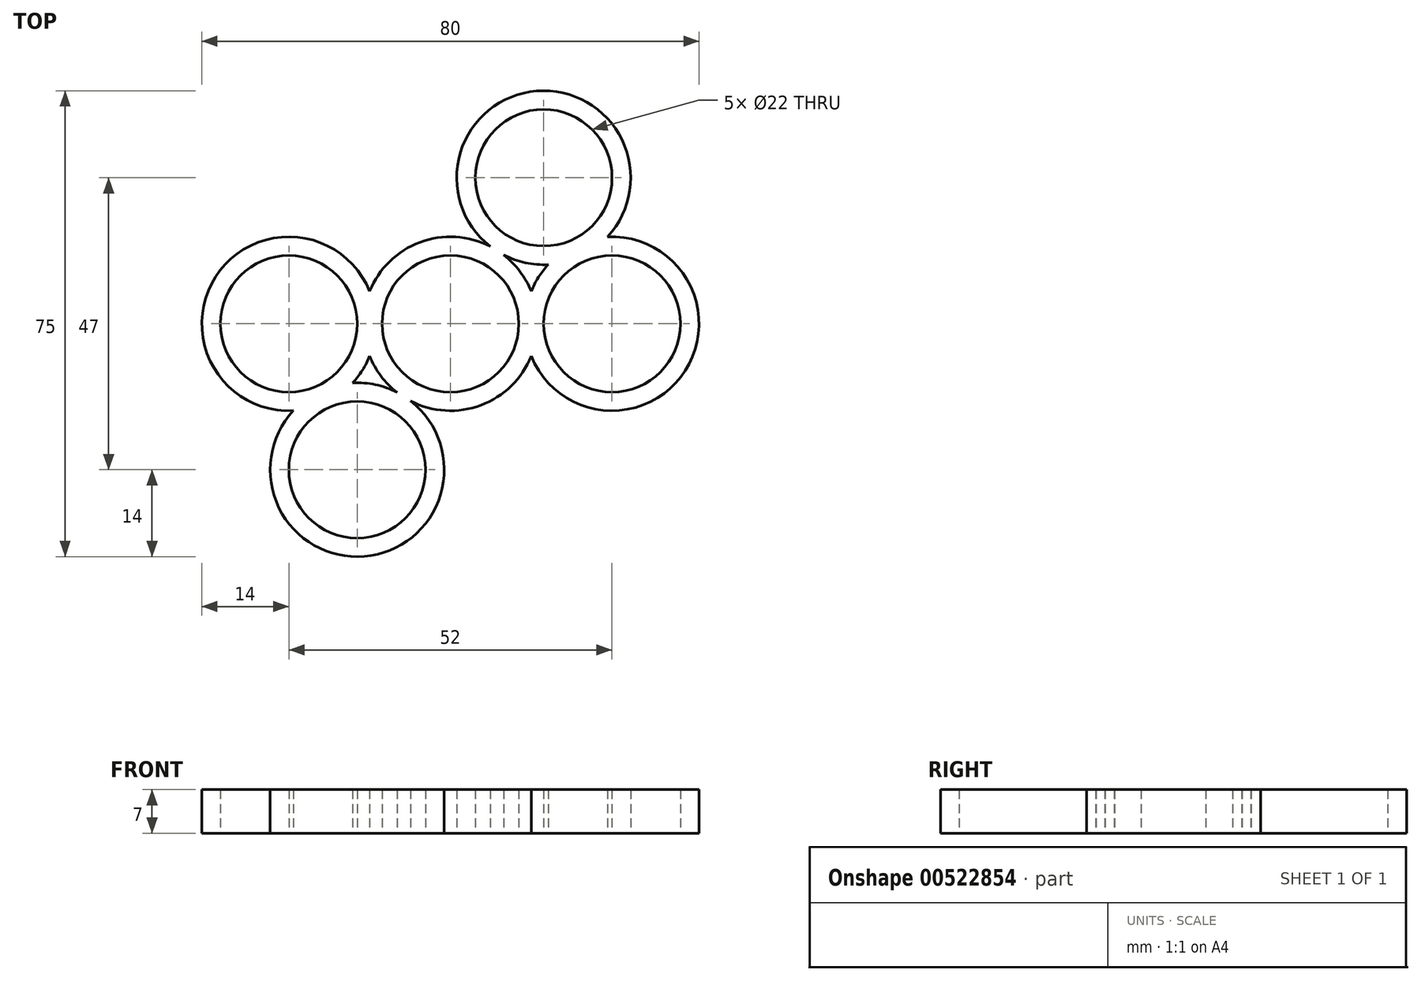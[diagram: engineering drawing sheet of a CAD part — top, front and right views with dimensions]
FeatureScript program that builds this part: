
annotation { "Feature Type Name" : "Feature", "Feature Type Description" : "" }
export const myFeature = defineFeature(function(context is Context, id is Id, definition is map)
    precondition{}
    {
        {
            var Q0;
            Q0=qCreatedBy(makeId("Top.planeOp"),FACE);
            var sketch = newSketch(context, id + "F0", { "sketchPlane" : qUnion([Q0])});
            skCircle(sketch, "E0", {"center": v(0, 0) * mm, "radius": 11 * mm});
            skCircle(sketch, "E1", {"center": v(26, 0) * mm, "radius": 11 * mm});
            skCircle(sketch, "E2", {"center": v(26, 0) * mm, "radius": 14 * mm});
            skCircle(sketch, "E3", {"center": v(0, 0) * mm, "radius": 14 * mm});
            skCircle(sketch, "E4", {"center": v(15, 23.5) * mm, "radius": 11 * mm});
            skCircle(sketch, "E5", {"center": v(15, 23.5) * mm, "radius": 14 * mm});
            skCircle(sketch, "E6", {"center": v(-26, 0) * mm, "radius": 11 * mm});
            skCircle(sketch, "E7", {"center": v(-26, 0) * mm, "radius": 14 * mm});
            skCircle(sketch, "E8", {"center": v(-15, -23.5) * mm, "radius": 11 * mm});
            skCircle(sketch, "E9", {"center": v(-15, -23.5) * mm, "radius": 14 * mm});
            skLineSegment(sketch, "E10", {"start": v(-1, -23.5) * mm, "end": v(-1, -13.96) * mm});
            skLineSegment(sketch, "E11", {"start": v(1, 23.5) * mm, "end": v(1, 13.96) * mm});
            skSolve(sketch);
        }
        {
            var Q0;
            Q0=makeQuery(id+"F0.imprint","IMPRINT",FACE,{"disambiguationData":[TD([[makeQuery(id+"F0.imprint","IMPRINT",EDGE,{"derivedFrom":sQuery(id+"F0.wireOp",EDGE,"E6")}),-1.0]])]});
            var Q1;
            Q1=makeQuery(id+"F0.imprint","IMPRINT",FACE,{"disambiguationData":[TD([[makeQuery(id+"F0.imprint","IMPRINT",EDGE,{"derivedFrom":sQuery(id+"F0.wireOp",EDGE,"E0")}),-1.0]])]});
            var Q2;
            {var subQ0=sQuery(id+"F0.wireOp",EDGE,"E7");var subQ1=sQuery(id+"F0.wireOp",EDGE,"E3");var subQ2=makeQuery(id+"F0.imprint","INTERSECT",VERTEX,{"disambiguationData":[OD(0.0)],"derivedFrom":[subQ1,subQ0]});Q2=makeQuery(id+"F0.imprint","IMPRINT",FACE,{"disambiguationData":[TD([[makeQuery(id+"F0.imprint","IMPRINT",EDGE,{"disambiguationData":[TD([[subQ2,-1.0]])],"derivedFrom":subQ1}),1.0]])]});}
            var Q3;
            {var subQ0=sQuery(id+"F0.wireOp",EDGE,"E9");var subQ1=sQuery(id+"F0.wireOp",EDGE,"E7");var subQ2=makeQuery(id+"F0.imprint","INTERSECT",VERTEX,{"disambiguationData":[OD(0.0)],"derivedFrom":[subQ1,subQ0]});Q3=makeQuery(id+"F0.imprint","IMPRINT",FACE,{"disambiguationData":[TD([[makeQuery(id+"F0.imprint","IMPRINT",EDGE,{"disambiguationData":[TD([[subQ2,-1.0]])],"derivedFrom":subQ1}),1.0]])]});}
            var Q4;
            Q4=makeQuery(id+"F0.imprint","IMPRINT",FACE,{"disambiguationData":[TD([[makeQuery(id+"F0.imprint","IMPRINT",EDGE,{"derivedFrom":sQuery(id+"F0.wireOp",EDGE,"E8")}),-1.0]])]});
            var Q5;
            {var subQ0=sQuery(id+"F0.wireOp",EDGE,"E3");var subQ1=sQuery(id+"F0.wireOp",EDGE,"E2");var subQ2=makeQuery(id+"F0.imprint","INTERSECT",VERTEX,{"disambiguationData":[OD(0.0)],"derivedFrom":[subQ1,subQ0]});Q5=makeQuery(id+"F0.imprint","IMPRINT",FACE,{"disambiguationData":[TD([[makeQuery(id+"F0.imprint","IMPRINT",EDGE,{"disambiguationData":[TD([[subQ2,1.0]])],"derivedFrom":subQ1}),1.0]])]});}
            var Q6;
            Q6=makeQuery(id+"F0.imprint","IMPRINT",FACE,{"disambiguationData":[TD([[makeQuery(id+"F0.imprint","IMPRINT",EDGE,{"derivedFrom":sQuery(id+"F0.wireOp",EDGE,"E1")}),-1.0]])]});
            var Q7;
            Q7=makeQuery(id+"F0.imprint","IMPRINT",FACE,{"disambiguationData":[TD([[makeQuery(id+"F0.imprint","IMPRINT",EDGE,{"derivedFrom":sQuery(id+"F0.wireOp",EDGE,"E4")}),-1.0]])]});
            var Q8;
            {var subQ0=sQuery(id+"F0.wireOp",EDGE,"E5");var subQ1=sQuery(id+"F0.wireOp",EDGE,"E2");var subQ2=makeQuery(id+"F0.imprint","INTERSECT",VERTEX,{"disambiguationData":[OD(0.0)],"derivedFrom":[subQ1,subQ0]});Q8=makeQuery(id+"F0.imprint","IMPRINT",FACE,{"disambiguationData":[TD([[makeQuery(id+"F0.imprint","IMPRINT",EDGE,{"disambiguationData":[TD([[subQ2,-1.0]])],"derivedFrom":subQ1}),1.0]])]});}
            var Q9;
            {var subQ0=sQuery(id+"F0.wireOp",EDGE,"E9");var subQ1=sQuery(id+"F0.wireOp",EDGE,"E3");var subQ2=makeQuery(id+"F0.imprint","INTERSECT",VERTEX,{"disambiguationData":[OD(0.0)],"derivedFrom":[subQ1,subQ0]});Q9=makeQuery(id+"F0.imprint","IMPRINT",FACE,{"disambiguationData":[TD([[makeQuery(id+"F0.imprint","IMPRINT",EDGE,{"disambiguationData":[TD([[subQ2,-1.0]])],"derivedFrom":subQ1}),1.0]])]});}
            var Q10;
            {var subQ0=sQuery(id+"F0.wireOp",EDGE,"E5");var subQ1=sQuery(id+"F0.wireOp",EDGE,"E3");var subQ2=makeQuery(id+"F0.imprint","INTERSECT",VERTEX,{"disambiguationData":[OD(0.0)],"derivedFrom":[subQ1,subQ0]});Q10=makeQuery(id+"F0.imprint","IMPRINT",FACE,{"disambiguationData":[TD([[makeQuery(id+"F0.imprint","IMPRINT",EDGE,{"disambiguationData":[TD([[subQ2,-1.0]])],"derivedFrom":subQ1}),1.0]])]});}
            extrude(context, id + "F1", {"entities" : qUnion([Q0, Q1, Q2, Q3, Q4, Q5, Q6, Q7, Q8, Q9, Q10]), "depth" : 7 * mm, "offsetDistance" : 25 * mm});
        }
    });
